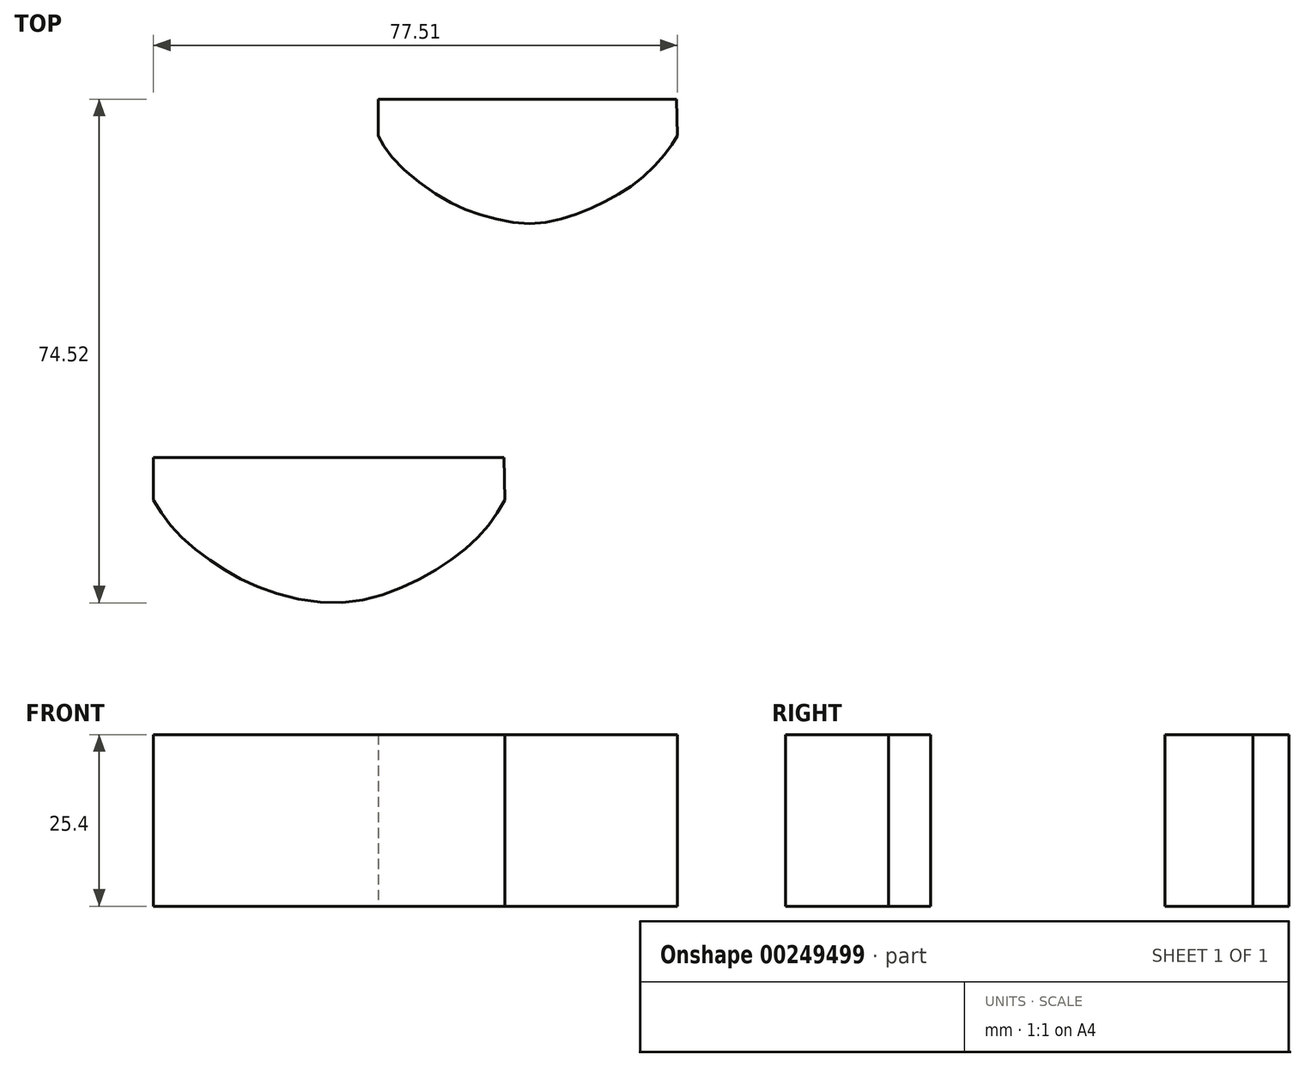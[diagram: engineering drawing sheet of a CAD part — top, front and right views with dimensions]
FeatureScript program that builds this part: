
annotation { "Feature Type Name" : "Feature", "Feature Type Description" : "" }
export const myFeature = defineFeature(function(context is Context, id is Id, definition is map)
    precondition{}
    {
        {
            var Q0;
            Q0=qCreatedBy(makeId("Top.planeOp"),FACE);
            var sketch = newSketch(context, id + "F0", { "sketchPlane" : qUnion([Q0])});
            skLineSegment(sketch, "E0", {"start": v(-53.75, 62) * mm, "end": v(-9.64, 62) * mm});
            skLineSegment(sketch, "E1", {"start": v(-53.75, 62) * mm, "end": v(-53.75, 56.62) * mm});
            skLineSegment(sketch, "E2", {"start": v(-53.75, 56.62) * mm, "end": v(-9.5, 56.62) * mm});
            skLineSegment(sketch, "E3", {"start": v(-9.5, 56.62) * mm, "end": v(-9.64, 62) * mm});
            skFitSpline(sketch, "E4", {"points": [v(-53.75, 56.62) * mm, v(-51.51, 53.14) * mm, v(-44.5, 47.53) * mm, v(-38.61, 44.92) * mm, v(-31.8, 43.6) * mm, v(-25.72, 44.54) * mm, v(-20.02, 46.97) * mm, v(-15.35, 49.87) * mm, v(-11.23, 53.98) * mm, v(-9.5, 56.62) * mm], "startDerivative": vector(17.87, -35.27) * mm, "endDerivative": vector(17.74, 30.54) * mm});
            skLineSegment(sketch, "E5", {"start": v(-87.02, 8.95) * mm, "end": v(-35.15, 8.95) * mm});
            skLineSegment(sketch, "E6", {"start": v(-87.02, 8.95) * mm, "end": v(-87.02, 2.7) * mm});
            skLineSegment(sketch, "E7", {"start": v(-87.02, 2.7) * mm, "end": v(-35, 2.7) * mm});
            skLineSegment(sketch, "E8", {"start": v(-35, 2.7) * mm, "end": v(-35.15, 8.95) * mm});
            skFitSpline(sketch, "E9", {"points": [v(-87.02, 2.7) * mm, v(-83.78, -1.9) * mm, v(-78.08, -6.6) * mm, v(-71.17, -10.33) * mm, v(-60.38, -12.53) * mm, v(-50.8, -10.48) * mm, v(-43.29, -6.38) * mm, v(-38.04, -1.82) * mm, v(-35, 2.7) * mm], "startDerivative": vector(26.59, -43.75) * mm, "endDerivative": vector(25.95, 43.85) * mm});
            skLineSegment(sketch, "E10", {"start": v(9.45, 41.93) * mm, "end": v(-100.76, 41.93) * mm, "construction": true});
            skLineSegment(sketch, "E11", {"start": v(-91.23, -12.15) * mm, "end": v(-15.23, -12.15) * mm, "construction": true});
            skSolve(sketch);
        }
        {
            var Q0;
            Q0=makeQuery(id+"F0.imprint","IMPRINT",FACE,{"disambiguationData":[TD([[makeQuery(id+"F0.imprint","IMPRINT",EDGE,{"derivedFrom":sQuery(id+"F0.wireOp",EDGE,"E0")}),-1.0]])]});
            var Q1;
            Q1=makeQuery(id+"F0.imprint","IMPRINT",FACE,{"disambiguationData":[TD([[makeQuery(id+"F0.imprint","IMPRINT",EDGE,{"derivedFrom":sQuery(id+"F0.wireOp",EDGE,"E2")}),-1.0]])]});
            var Q2;
            Q2=makeQuery(id+"F0.imprint","IMPRINT",FACE,{"disambiguationData":[TD([[makeQuery(id+"F0.imprint","IMPRINT",EDGE,{"derivedFrom":sQuery(id+"F0.wireOp",EDGE,"E5")}),-1.0]])]});
            var Q3;
            Q3=makeQuery(id+"F0.imprint","IMPRINT",FACE,{"disambiguationData":[TD([[makeQuery(id+"F0.imprint","IMPRINT",EDGE,{"derivedFrom":sQuery(id+"F0.wireOp",EDGE,"E7")}),-1.0]])]});
            extrude(context, id + "F1", {"entities" : qUnion([Q0, Q1, Q2, Q3]), "depth" : 25.4 * mm});
        }
    });
